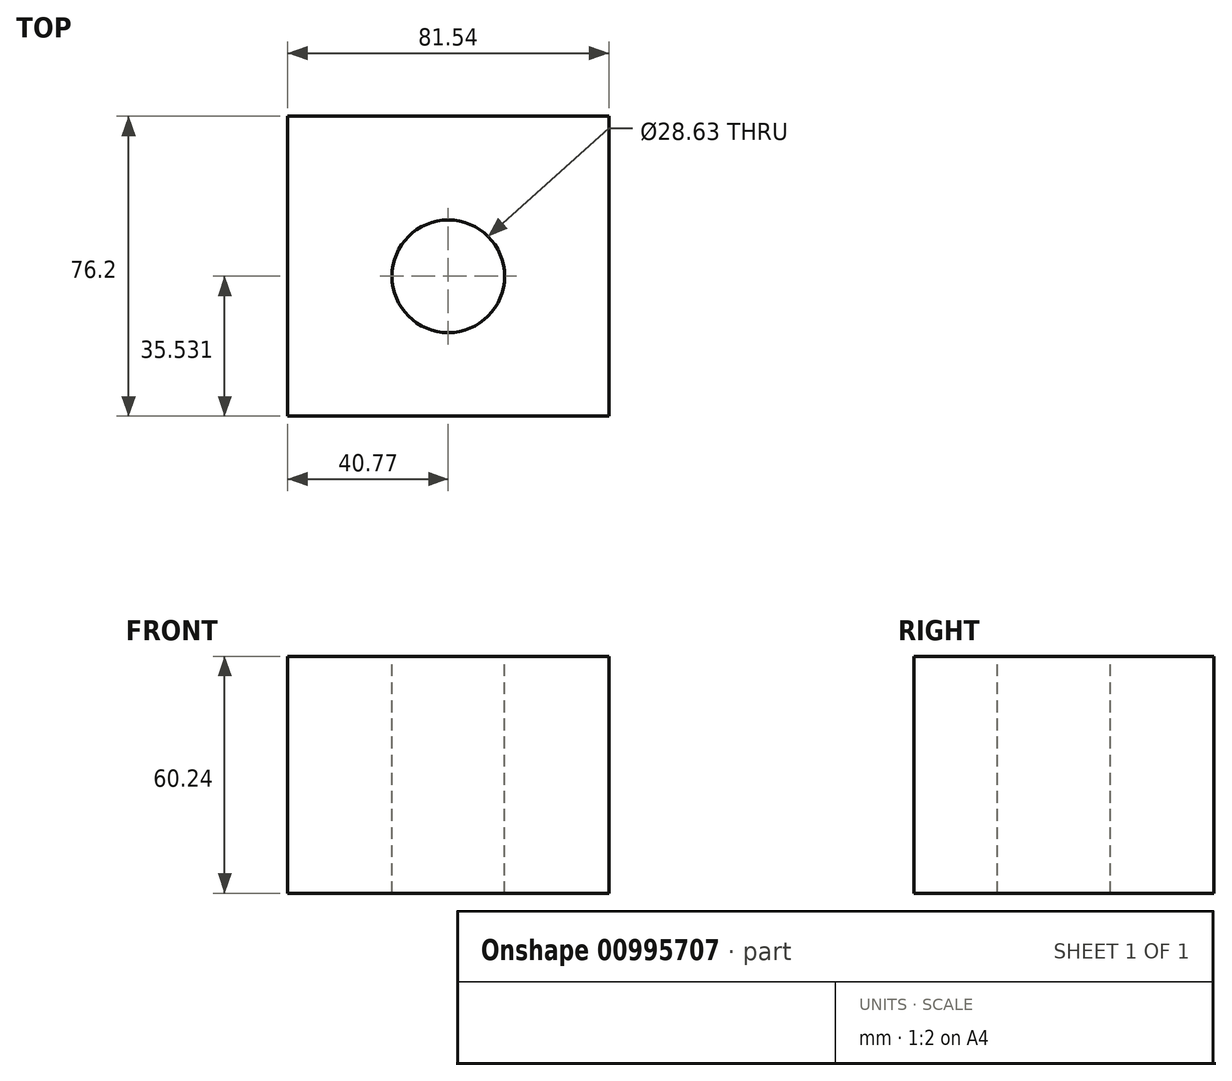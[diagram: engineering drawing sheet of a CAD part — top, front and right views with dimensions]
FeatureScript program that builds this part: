
annotation { "Feature Type Name" : "Feature", "Feature Type Description" : "" }
export const myFeature = defineFeature(function(context is Context, id is Id, definition is map)
    precondition{}
    {
        {
            var Q0;
            Q0=qCreatedBy(makeId("Front.planeOp"),FACE);
            var sketch = newSketch(context, id + "F0", { "sketchPlane" : qUnion([Q0])});
            skLineSegment(sketch, "E0.bottom", {"start": v(40.77, 30.12) * mm, "end": v(-40.77, 30.12) * mm});
            skLineSegment(sketch, "E0.top", {"start": v(40.77, -30.12) * mm, "end": v(-40.77, -30.12) * mm});
            skLineSegment(sketch, "E0.left", {"start": v(40.77, 30.12) * mm, "end": v(40.77, -30.12) * mm});
            skLineSegment(sketch, "E0.right", {"start": v(-40.77, 30.12) * mm, "end": v(-40.77, -30.12) * mm});
            skPoint(sketch, "E0.middle", {"position": v(0, 0) * mm});
            skSolve(sketch);
        }
        {
            var Q0;
            Q0=makeQuery(id+"F0.imprint","IMPRINT",FACE,{"disambiguationData":[TD([[makeQuery(id+"F0.imprint","IMPRINT",EDGE,{"derivedFrom":sQuery(id+"F0.wireOp",EDGE,"E0.bottom")}),1.0]])]});
            extrude(context, id + "F1", {"entities" : qUnion([Q0]), "depth" : 76.2 * mm, "offsetDistance" : 25.4 * mm});
        }
        {
            var Q0;
            Q0=makeQuery(id+"F1.opExtrude","SWEPT_FACE",FACE,{"disambiguationData":[OSD([sQuery(id+"F0.wireOp",EDGE,"E0.bottom")])]});
            var sketch = newSketch(context, id + "F2", { "sketchPlane" : qUnion([Q0])});
            skCircle(sketch, "E1", {"center": v(0, -40.67) * mm, "radius": 14.31 * mm});
            skSolve(sketch);
        }
        {
            var Q0;
            Q0=makeQuery(id+"F2.imprint","IMPRINT",FACE,{"disambiguationData":[TD([[makeQuery(id+"F2.imprint","IMPRINT",EDGE,{"derivedFrom":sQuery(id+"F2.wireOp",EDGE,"E1")}),1.0]])]});
            extrude(context, id + "F3", {"entities" : qUnion([Q0]), "operationType" : NewBodyOperationType.REMOVE, "endBound" : BoundingType.SYMMETRIC, "oppositeDirection" : true, "depth" : 127 * mm, "offsetDistance" : 25.4 * mm});
        }
    });
